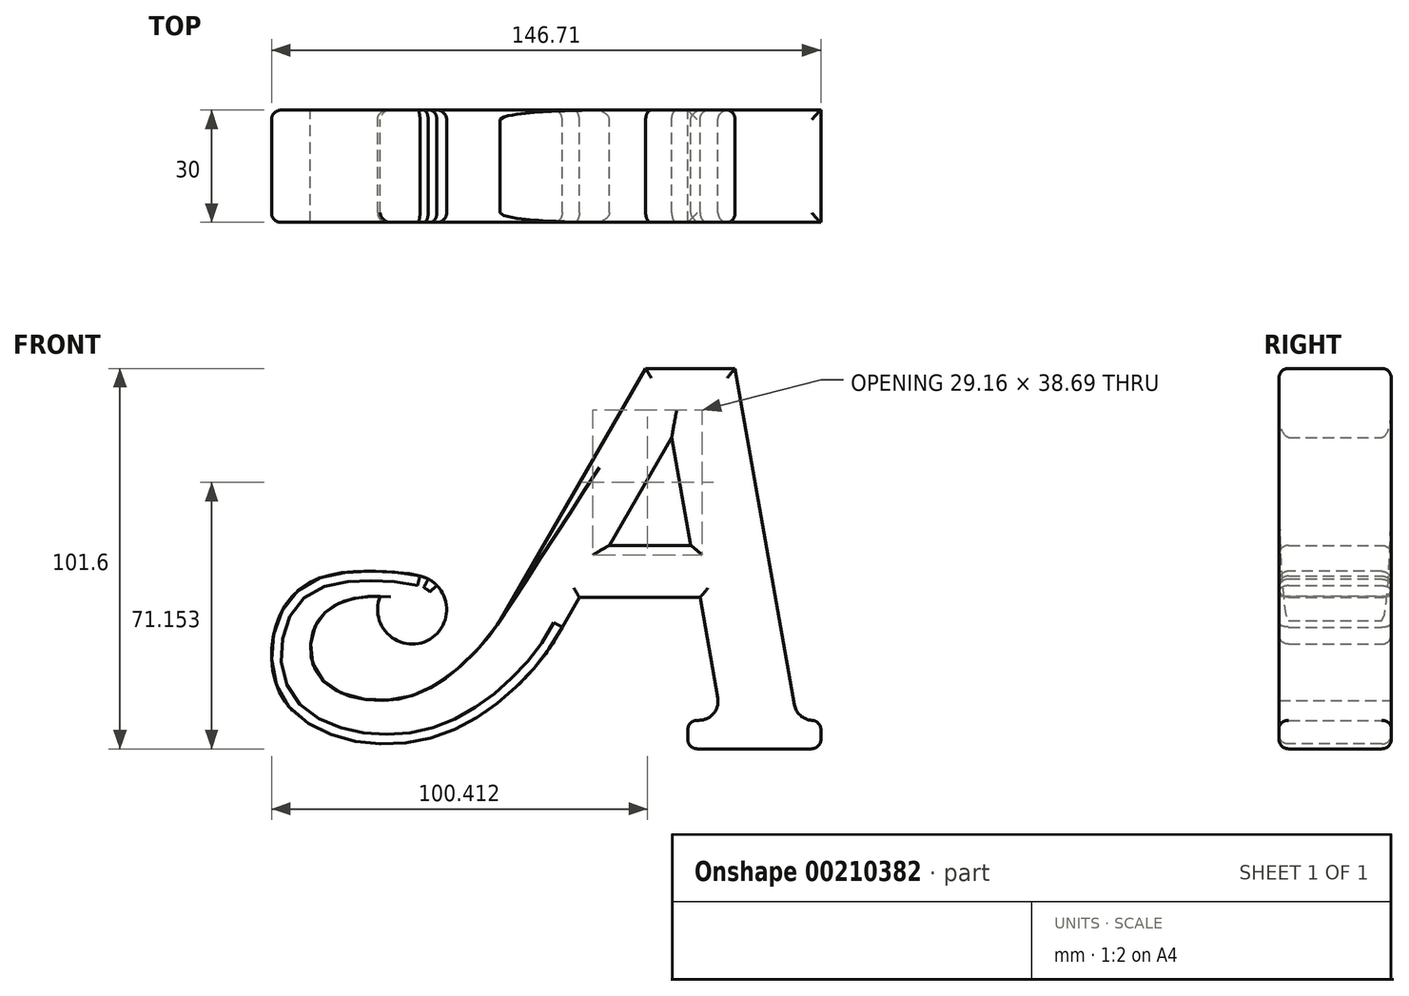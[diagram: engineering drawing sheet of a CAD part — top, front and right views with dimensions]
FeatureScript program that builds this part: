
annotation { "Feature Type Name" : "Feature", "Feature Type Description" : "" }
export const myFeature = defineFeature(function(context is Context, id is Id, definition is map)
    precondition{}
    {
        {
            var Q0;
            Q0=qCreatedBy(makeId("Front.planeOp"),FACE);
            var sketch = newSketch(context, id + "F0", { "sketchPlane" : qUnion([Q0])});
            skLineSegment(sketch, "E0", {"start": v(28, 0) * mm, "end": v(28, 7.62) * mm});
            skLineSegment(sketch, "E1", {"start": v(28, 7.62) * mm, "end": v(25.9, 7.62) * mm});
            skLineSegment(sketch, "E2", {"start": v(20.9, 11.82) * mm, "end": v(5.07, 101.6) * mm});
            skLineSegment(sketch, "E3", {"start": v(5.07, 101.6) * mm, "end": v(-18.8, 101.6) * mm});
            skLineSegment(sketch, "E4", {"start": v(-18.8, 101.6) * mm, "end": v(-57.72, 34.2) * mm});
            skLineSegment(sketch, "E5", {"start": v(0.43, 13.58) * mm, "end": v(-4.3, 40.43) * mm});
            skLineSegment(sketch, "E6", {"start": v(-11.84, 83.19) * mm, "end": v(-28.49, 54.35) * mm});
            skFitSpline(sketch, "E7", {"points": [v(-41.09, 32.52) * mm, v(-74.94, 3.25) * mm, v(-115.48, 13.2) * mm, v(-112.86, 41.17) * mm, v(-89.58, 47.36) * mm, v(-73.81, 42.37) * mm, v(-78.65, 31.45) * mm, v(-87.86, 34.24) * mm, v(-90.25, 37.19) * mm], "startDerivative": vector(-77.48, -156.3) * mm, "endDerivative": vector(-117.67, 2.02) * mm});
            skFitSpline(sketch, "E8", {"points": [v(-55.51, 38.02) * mm, v(-72.17, 18.88) * mm, v(-90.67, 12.91) * mm, v(-105.58, 18.88) * mm, v(-107.97, 30.22) * mm, v(-103, 37.57) * mm, v(-94.45, 40.56) * mm, v(-85.7, 39.76) * mm, v(-83.9, 35.98) * mm], "startDerivative": vector(-52, -104.19) * mm, "endDerivative": vector(11.45, -68.03) * mm});
            skArc(sketch, "E9", {"start": v(-89.66, 40.75) * mm, "mid": v(-76.98, 28.98) * mm, "end": v(-79.07, 46.16) * mm});
            skLineSegment(sketch, "E10", {"start": v(-28.49, 54.35) * mm, "end": v(-6.75, 54.35) * mm});
            skLineSegment(sketch, "E11", {"start": v(-36.52, 40.43) * mm, "end": v(-4.3, 40.43) * mm});
            skLineSegment(sketch, "E12.trimOffspring", {"start": v(-6.75, 54.35) * mm, "end": v(-11.84, 83.19) * mm});
            skLineSegment(sketch, "E13.trimOffspring", {"start": v(-36.52, 40.43) * mm, "end": v(-41.09, 32.52) * mm});
            skLineSegment(sketch, "E14", {"start": v(28, 0) * mm, "end": v(-7.57, 0) * mm});
            skLineSegment(sketch, "E15", {"start": v(-7.57, 0) * mm, "end": v(-7.57, 7.62) * mm});
            skLineSegment(sketch, "E16", {"start": v(-7.57, 7.62) * mm, "end": v(-4.57, 7.62) * mm});
            skPoint(sketch, "E17.start.orphan", {"position": v(0, 7.62) * mm});
            skPoint(sketch, "E18.visualSharp", {"position": v(21.64, 7.62) * mm});
            skArc(sketch, "E18.filletArc", {"start": v(20.9, 11.82) * mm, "mid": v(22.64, 8.8) * mm, "end": v(25.9, 7.62) * mm});
            skPoint(sketch, "E19.visualSharp", {"position": v(1.49, 7.62) * mm});
            skArc(sketch, "E19.filletArc", {"start": v(-4.57, 7.62) * mm, "mid": v(-0.68, 9.43) * mm, "end": v(0.43, 13.58) * mm});
            skSolve(sketch);
        }
        {
            var Q0;
            Q0 = qSketchRegion(id + "F0", true);
            extrude(context, id + "F1", {"entities" : qUnion([Q0]), "depth" : 30 * mm});
        }
        {
            var Q0;
            Q0=makeQuery(id+"F1.opExtrude","CAP_EDGE",EDGE,{"disambiguationData":[OSD([sQuery(id+"F0.wireOp",EDGE,"E7")])],"isStart":false});
            var Q1;
            Q1=makeQuery(id+"F1.opExtrude","CAP_EDGE",EDGE,{"disambiguationData":[OSD([sQuery(id+"F0.wireOp",EDGE,"E7")])],"isStart":true});
            var Q2;
            Q2=makeQuery(id+"F1.opExtrude","CAP_EDGE",EDGE,{"disambiguationData":[OSD([sQuery(id+"F0.wireOp",EDGE,"E9")])],"isStart":true});
            var Q3;
            Q3=makeQuery(id+"F1.opExtrude","CAP_EDGE",EDGE,{"disambiguationData":[OSD([sQuery(id+"F0.wireOp",EDGE,"E9")])],"isStart":false});
            var Q4;
            Q4=makeQuery(id+"F1.opExtrude","CAP_EDGE",EDGE,{"disambiguationData":[OSD([sQuery(id+"F0.wireOp",EDGE,"E4")])],"isStart":false});
            var Q5;
            Q5=makeQuery(id+"F1.opExtrude","CAP_EDGE",EDGE,{"disambiguationData":[OSD([sQuery(id+"F0.wireOp",EDGE,"E4")])],"isStart":true});
            var Q6;
            Q6=makeQuery(id+"F1.opExtrude","CAP_EDGE",EDGE,{"disambiguationData":[OSD([sQuery(id+"F0.wireOp",EDGE,"E3")])],"isStart":false});
            var Q7;
            Q7=makeQuery(id+"F1.opExtrude","CAP_EDGE",EDGE,{"disambiguationData":[OSD([sQuery(id+"F0.wireOp",EDGE,"E2")])],"isStart":false});
            var Q8;
            Q8=makeQuery(id+"F1.opExtrude","CAP_EDGE",EDGE,{"disambiguationData":[OSD([sQuery(id+"F0.wireOp",EDGE,"E6")])],"isStart":false});
            var Q9;
            Q9=makeQuery(id+"F1.opExtrude","CAP_EDGE",EDGE,{"disambiguationData":[OSD([sQuery(id+"F0.wireOp",EDGE,"E12.trimOffspring")])],"isStart":false});
            var Q10;
            Q10=makeQuery(id+"F1.opExtrude","CAP_EDGE",EDGE,{"disambiguationData":[OSD([sQuery(id+"F0.wireOp",EDGE,"E10")])],"isStart":false});
            var Q11;
            Q11=makeQuery(id+"F1.opExtrude","CAP_EDGE",EDGE,{"disambiguationData":[OSD([sQuery(id+"F0.wireOp",EDGE,"E3")])],"isStart":true});
            var Q12;
            Q12=makeQuery(id+"F1.opExtrude","CAP_EDGE",EDGE,{"disambiguationData":[OSD([sQuery(id+"F0.wireOp",EDGE,"E2")])],"isStart":true});
            var Q13;
            Q13=makeQuery(id+"F1.opExtrude","CAP_EDGE",EDGE,{"disambiguationData":[OSD([sQuery(id+"F0.wireOp",EDGE,"E12.trimOffspring")])],"isStart":true});
            var Q14;
            Q14=makeQuery(id+"F1.opExtrude","CAP_EDGE",EDGE,{"disambiguationData":[OSD([sQuery(id+"F0.wireOp",EDGE,"E6")])],"isStart":true});
            var Q15;
            Q15=makeQuery(id+"F1.opExtrude","CAP_EDGE",EDGE,{"disambiguationData":[OSD([sQuery(id+"F0.wireOp",EDGE,"E10")])],"isStart":true});
            var Q16;
            Q16=makeQuery(id+"F1.opExtrude","CAP_EDGE",EDGE,{"disambiguationData":[OSD([sQuery(id+"F0.wireOp",EDGE,"E11")])],"isStart":true});
            var Q17;
            Q17=makeQuery(id+"F1.opExtrude","CAP_EDGE",EDGE,{"disambiguationData":[OSD([sQuery(id+"F0.wireOp",EDGE,"E11")])],"isStart":false});
            var Q18;
            Q18=makeQuery(id+"F1.opExtrude","CAP_EDGE",EDGE,{"disambiguationData":[OSD([sQuery(id+"F0.wireOp",EDGE,"E5")])],"isStart":false});
            var Q19;
            Q19=makeQuery(id+"F1.opExtrude","CAP_EDGE",EDGE,{"disambiguationData":[OSD([sQuery(id+"F0.wireOp",EDGE,"E5")])],"isStart":true});
            var Q20;
            Q20=makeQuery(id+"F1.opExtrude","SWEPT_EDGE",EDGE,{"disambiguationData":[OSD([sQuery(id+"F0.wireOp",EDGE,"E15"),sQuery(id+"F0.wireOp",EDGE,"E16")])]});
            var Q21;
            Q21=makeQuery(id+"F1.opExtrude","SWEPT_EDGE",EDGE,{"disambiguationData":[OSD([sQuery(id+"F0.wireOp",EDGE,"E0"),sQuery(id+"F0.wireOp",EDGE,"E1")])]});
            var Q22;
            Q22=makeQuery(id+"F1.opExtrude","CAP_EDGE",EDGE,{"disambiguationData":[OSD([sQuery(id+"F0.wireOp",EDGE,"E14")])],"isStart":false});
            var Q23;
            Q23=makeQuery(id+"F1.opExtrude","SWEPT_EDGE",EDGE,{"disambiguationData":[OSD([sQuery(id+"F0.wireOp",EDGE,"E0"),sQuery(id+"F0.wireOp",EDGE,"E14")])]});
            var Q24;
            Q24=makeQuery(id+"F1.opExtrude","CAP_EDGE",EDGE,{"disambiguationData":[OSD([sQuery(id+"F0.wireOp",EDGE,"E14")])],"isStart":true});
            var Q25;
            Q25=makeQuery(id+"F1.opExtrude","SWEPT_EDGE",EDGE,{"disambiguationData":[OSD([sQuery(id+"F0.wireOp",EDGE,"E14"),sQuery(id+"F0.wireOp",EDGE,"E15")])]});
            fillet(context, id + "F2", {"entities" : qUnion([Q0, Q1, Q2, Q3, Q4, Q5, Q6, Q7, Q8, Q9, Q10, Q11, Q12, Q13, Q14, Q15, Q16, Q17, Q18, Q19, Q20, Q21, Q22, Q23, Q24, Q25]), "radius" : 2.54 * mm, "tangentPropagation" : true, "allowEdgeOverflow" : false});
        }
    });
